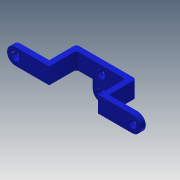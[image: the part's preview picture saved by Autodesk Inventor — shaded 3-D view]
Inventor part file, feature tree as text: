
AUTODESK INVENTOR PART (.ipt)
format: ipt  version: 2013 (Build 170138000, 138)  size: 219,648 bytes
history: native  units: mm
features: sketch x15, extrude x14, fillet x1
ambient origin geometry x8: Origin, YZ Plane, XZ Plane, XY Plane, X Axis, Y Axis, Z Axis, Center Point
bodies: Solid1 (feature_tree)
feature tree (30):
  extrude  "Extrusion1"  Depth=6.0mm
  extrude  "Extrusion2"  Depth=2.0mm
  sketch  "Sketch3"  dims[d5=2.0mm d6=10.0mm d7=0.0mm]
  extrude  "Extrusion3"  Depth=10.0mm TaperAngle=0.0deg
  extrude  "Extrusion4"  Depth=2.0mm
  sketch  "Sketch5"  dims[d10=6.0mm d11=2.0mm]
  sketch  "Sketch6"  dims[d12=14.0mm d13=0.0mm d14=14.0mm d15=0.0mm]
  extrude  "Extrusion5"  Depth=2.0mm
  extrude  "Extrusion6"  Depth=14.0mm TaperAngle=0.0deg
  extrude  "Extrusion7"  Depth=3.5mm
  extrude  "Extrusion8"  Depth=2.0mm TaperAngle=0.0deg
  fillet  "Fillet1"  Radius=3.0mm
  extrude  "Extrusion9"  Depth=3.0mm
  extrude  "Extrusion10"  Depth=1.0mm
  extrude  "Extrusion11"  Depth=3.0mm
  extrude  "Extrusion12"  Depth=6.0mm
  extrude  "Extrusion13"  Depth=3.0mm
  extrude  "Extrusion14"  Depth=2.0mm TaperAngle=0.0deg
  sketch  "Sketch15"  dims[d41=2.0mm d42=0.0mm d44=3.0mm d45=6.0mm d46=2.0mm d47=0.0mm d48=3.0mm d49=2.0mm d50=0.0mm]
  sketch  "Sketch1"  dims[d0=22.0mm d1=6.0mm]
  sketch  "Sketch2"  dims[d2=2.0mm d3=0.0mm d4=2.0mm]
  sketch  "Sketch4"  dims[d8=6.0mm d9=2.0mm]
  sketch  "Sketch7"  dims[d16=3.5mm d17=3.5mm]
  sketch  "Sketch8"  dims[d18=2.0mm d19=0.0mm d20=2.0mm d21=0.0mm d22=3.0mm]
  sketch  "Sketch9"  dims[d23=2.0mm d24=0.0mm d25=3.0mm]
  sketch  "Sketch10"  dims[d26=2.0mm d27=0.0mm d28=1.0mm]
  sketch  "Sketch11"  dims[d29=3.0mm d30=3.0mm]
  sketch  "Sketch12"  dims[d31=2.0mm d32=0.0mm d33=6.0mm]
  sketch  "Sketch13"  dims[d34=3.0mm d35=3.0mm]
  sketch  "Sketch14"  dims[d37=2.0mm d38=0.0mm d39=2.0mm d40=0.0mm]
